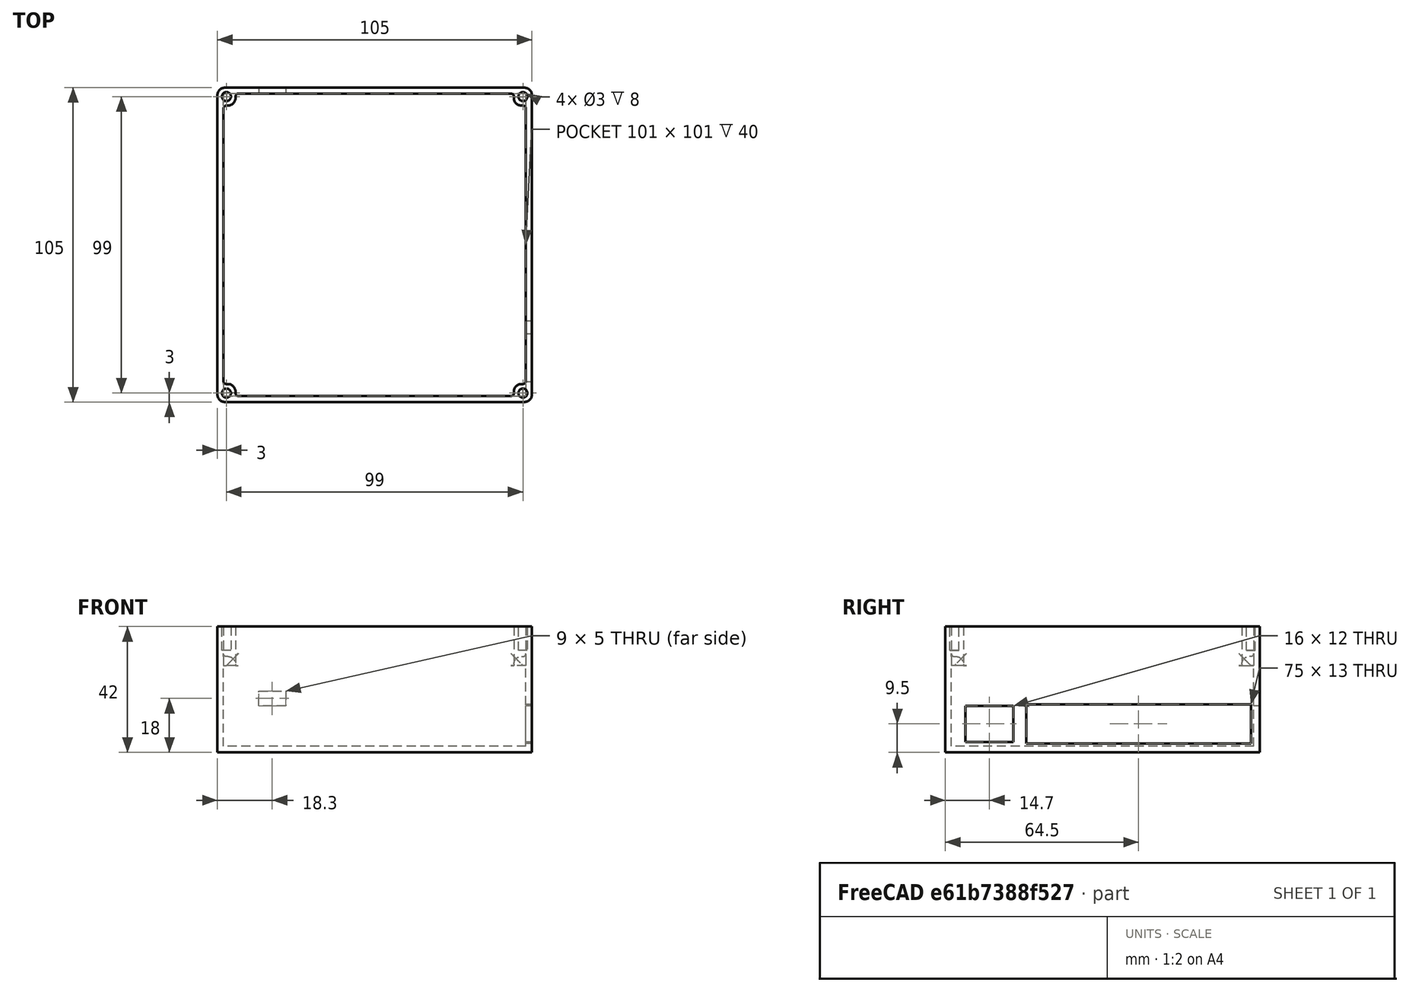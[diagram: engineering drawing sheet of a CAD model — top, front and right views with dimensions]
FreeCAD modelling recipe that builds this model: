
FCSTD DOCUMENT  (FreeCAD 0.19RUnknown)
Label: gdas_frame
License: All rights reserved
LicenseURL: http://en.wikipedia.org/wiki/All_rights_reserved
objects: Sketcher::SketchObject×6, PartDesign::Pad×3, PartDesign::Pocket×3, PartDesign::Fillet×3, PartDesign::Body×2, Mesh::Feature×1, App::MeasureDistance×1, PartDesign::Plane×1, PartDesign::Chamfer×1
note: 29 computed .brp shape members not serialized (recipe doc carries the construction recipe); baked Part::Feature solids carry a one-line shape summary decoded from their .brp

FEATURE [Mesh::Feature] OBJ_PCB_v2
  Placement = pos=(-1028.5,987.5,3) rot=(0,0,1;0rad)
FEATURE [PartDesign::Body] Body
  Origin = -> Origin
FEATURE [App::MeasureDistance] Distance  label="Distance: 97.20 mm"
  Distance = 97.1998
  P1 = (-48.7548,48.251,2.5)
  P2 = (48.4449,48.251,2.5)
FEATURE [Sketcher::SketchObject] Sketch
  MapMode = 5
  Support = -> [XY_Plane001]
  sketch-geometry (4):
    g0: LineSegment StartX=0 StartY=105 StartZ=0 EndX=105 EndY=105 EndZ=0
    g1: LineSegment StartX=105 StartY=105 StartZ=0 EndX=105 EndY=0 EndZ=0
    g2: LineSegment StartX=105 StartY=0 StartZ=0 EndX=0 EndY=0 EndZ=0
    g3: LineSegment StartX=0 StartY=0 StartZ=0 EndX=0 EndY=105 EndZ=0
  constraints (11):
    c: Coincident(g0,g1)
    c: Coincident(g1,g2)
    c: Coincident(g2,g3)
    c: Coincident(g3,g0)
    c: Horizontal(g0)
    c: Horizontal(g2)
    c: Vertical(g1)
    c: Vertical(g3)
    c: Coincident(g2,g-1)
    c: Distance(g0) = 105
    c: Distance(g1) = 105
FEATURE [PartDesign::Pad] Pad
  Direction = (1,1,1)
  Length = 2
  Length2 = 100
  Profile = -> Sketch
  Refine = true
  Type = 0
FEATURE [Sketcher::SketchObject] Sketch001
  ExternalGeometry = -> [Sketch]
  MapMode = 5
  Placement = pos=(0,0,2) rot=(0,0,1;0rad)
  Support = -> [Pad]
  sketch-geometry (8):
    g0: LineSegment StartX=0 StartY=0 StartZ=0 EndX=105 EndY=0 EndZ=0
    g1: LineSegment StartX=105 StartY=0 StartZ=0 EndX=105 EndY=105 EndZ=0
    g2: LineSegment StartX=105 StartY=105 StartZ=0 EndX=0 EndY=105 EndZ=0
    g3: LineSegment StartX=0 StartY=105 StartZ=0 EndX=0 EndY=0 EndZ=0
    g4: LineSegment StartX=2 StartY=2 StartZ=0 EndX=103 EndY=2 EndZ=0
    g5: LineSegment StartX=103 StartY=2 StartZ=0 EndX=103 EndY=103 EndZ=0
    g6: LineSegment StartX=103 StartY=103 StartZ=0 EndX=2 EndY=103 EndZ=0
    g7: LineSegment StartX=2 StartY=103 StartZ=0 EndX=2 EndY=2 EndZ=0
  constraints (22):
    c: Coincident(g0,g1)
    c: Coincident(g1,g2)
    c: Coincident(g2,g3)
    c: Coincident(g3,g0)
    c: Horizontal(g0)
    c: Horizontal(g2)
    c: Vertical(g1)
    c: Vertical(g3)
    c: Coincident(g0,g-1)
    c: Coincident(g1,g-3)
    c: Coincident(g4,g5)
    c: Coincident(g5,g6)
    c: Coincident(g6,g7)
    c: Coincident(g7,g4)
    c: Horizontal(g4)
    c: Horizontal(g6)
    c: Vertical(g5)
    c: Vertical(g7)
    c: Distance(g5) = 101
    c: Distance(g4) = 101
    c: DistanceX(g0,g4) = 2
    c: DistanceY(g0,g4) = 2
FEATURE [PartDesign::Pad] Pad001
  BaseFeature = -> Pad
  Direction = (1,1,1)
  Length = 40
  Length2 = 100
  Profile = -> Sketch001
  Refine = true
  Type = 0
FEATURE [Sketcher::SketchObject] Sketch002
  ExternalGeometry = -> [Pad001,Sketch]
  MapMode = 5
  Placement = pos=(105,0,0) rot=(0.57735,0.57735,0.57735;2.0944rad)
  Support = -> [Pad001]
  sketch-geometry (8):
    g0: LineSegment StartX=27 StartY=16 StartZ=0 EndX=102 EndY=16 EndZ=0
    g1: LineSegment StartX=102 StartY=16 StartZ=0 EndX=102 EndY=3 EndZ=0
    g2: LineSegment StartX=102 StartY=3 StartZ=0 EndX=27 EndY=3 EndZ=0
    g3: LineSegment StartX=27 StartY=3 StartZ=0 EndX=27 EndY=16 EndZ=0
    g4: LineSegment StartX=6.7 StartY=15.5 StartZ=0 EndX=22.7 EndY=15.5 EndZ=0
    g5: LineSegment StartX=22.7 StartY=15.5 StartZ=0 EndX=22.7 EndY=3.5 EndZ=0
    g6: LineSegment StartX=22.7 StartY=3.5 StartZ=0 EndX=6.7 EndY=3.5 EndZ=0
    g7: LineSegment StartX=6.7 StartY=3.5 StartZ=0 EndX=6.7 EndY=15.5 EndZ=0
  constraints (24):
    c: Coincident(g0,g1)
    c: Coincident(g1,g2)
    c: Coincident(g2,g3)
    c: Coincident(g3,g0)
    c: Horizontal(g0)
    c: Horizontal(g2)
    c: Vertical(g1)
    c: Vertical(g3)
    c: DistanceY(g-5,g1) = 3
    c: Distance(g1) = 13
    c: Distance(g0) = 75
    c: DistanceX(g1,g-5) = 3
    c: Coincident(g4,g5)
    c: Coincident(g5,g6)
    c: Coincident(g6,g7)
    c: Coincident(g7,g4)
    c: Horizontal(g4)
    c: Horizontal(g6)
    c: Vertical(g5)
    c: Vertical(g7)
    c: DistanceX(g-1,g6) = 6.7
    c: DistanceY(g-1,g6) = 3.5
    c: Distance(g4) = 16
    c: Distance(g7) = 12
FEATURE [PartDesign::Pocket] Pocket
  BaseFeature = -> Pad001
  Length = 0
  Length2 = 100
  Profile = -> Sketch002
  Refine = true
  Type = 2
FEATURE [Sketcher::SketchObject] Sketch003
  ExternalGeometry = -> [Pocket,Sketch]
  MapMode = 5
  Placement = pos=(0,105,0) rot=(0,0.707107,0.707107;3.14159rad)
  Support = -> [Pocket]
  sketch-geometry (4):
    g0: LineSegment StartX=-22.8 StartY=20.5 StartZ=0 EndX=-13.8 EndY=20.5 EndZ=0
    g1: LineSegment StartX=-13.8 StartY=20.5 StartZ=0 EndX=-13.8 EndY=15.5 EndZ=0
    g2: LineSegment StartX=-13.8 StartY=15.5 StartZ=0 EndX=-22.8 EndY=15.5 EndZ=0
    g3: LineSegment StartX=-22.8 StartY=15.5 StartZ=0 EndX=-22.8 EndY=20.5 EndZ=0
  constraints (12):
    c: Coincident(g0,g1)
    c: Coincident(g1,g2)
    c: Coincident(g2,g3)
    c: Coincident(g3,g0)
    c: Horizontal(g0)
    c: Horizontal(g2)
    c: Vertical(g1)
    c: Vertical(g3)
    c: DistanceX(g0,g0) = 9
    c: Distance(g1) = 5
    c: DistanceX(g1,g-1) = 13.8
    c: DistanceY(g-1,g1) = 15.5
FEATURE [PartDesign::Pocket] Pocket001
  BaseFeature = -> Pocket
  Length = 5
  Length2 = 100
  Profile = -> Sketch003
  Refine = true
  Type = 2
FEATURE [PartDesign::Plane] DatumPlane
  Length = 156
  MapMode = 5
  Placement = pos=(0,0,42) rot=(0,0,1;0rad)
  ResizeMode = 0
  Support = -> [Pocket001]
  Width = 156
FEATURE [Sketcher::SketchObject] Sketch004
  ExternalGeometry = -> [Pocket001]
  MapMode = 5
  Placement = pos=(0,0,42) rot=(0,0,1;0rad)
  Support = -> [Pocket001]
  sketch-geometry (16):
    g0: LineSegment StartX=103 StartY=103 StartZ=0 EndX=99 EndY=103 EndZ=0
    g1: LineSegment StartX=99 StartY=103 StartZ=0 EndX=99 EndY=99 EndZ=0
    g2: LineSegment StartX=99 StartY=99 StartZ=0 EndX=103 EndY=99 EndZ=0
    g3: LineSegment StartX=103 StartY=99 StartZ=0 EndX=103 EndY=103 EndZ=0
    g4: LineSegment StartX=103 StartY=2 StartZ=0 EndX=99 EndY=2 EndZ=0
    g5: LineSegment StartX=99 StartY=2 StartZ=0 EndX=99 EndY=6 EndZ=0
    g6: LineSegment StartX=99 StartY=6 StartZ=0 EndX=103 EndY=6 EndZ=0
    g7: LineSegment StartX=103 StartY=6 StartZ=0 EndX=103 EndY=2 EndZ=0
    g8: LineSegment StartX=2 StartY=2 StartZ=0 EndX=6 EndY=2 EndZ=0
    g9: LineSegment StartX=6 StartY=2 StartZ=0 EndX=6 EndY=6 EndZ=0
    g10: LineSegment StartX=6 StartY=6 StartZ=0 EndX=2 EndY=6 EndZ=0
    g11: LineSegment StartX=2 StartY=6 StartZ=0 EndX=2 EndY=2 EndZ=0
    g12: LineSegment StartX=2 StartY=103 StartZ=0 EndX=6 EndY=103 EndZ=0
    g13: LineSegment StartX=6 StartY=103 StartZ=0 EndX=6 EndY=99 EndZ=0
    g14: LineSegment StartX=6 StartY=99 StartZ=0 EndX=2 EndY=99 EndZ=0
    g15: LineSegment StartX=2 StartY=99 StartZ=0 EndX=2 EndY=103 EndZ=0
  constraints (44):
    c: Coincident(g0,g1)
    c: Coincident(g1,g2)
    c: Coincident(g2,g3)
    c: Coincident(g3,g0)
    c: Horizontal(g0)
    c: Horizontal(g2)
    c: Vertical(g1)
    c: Vertical(g3)
    c: Coincident(g0,g-4)
    c: Coincident(g4,g5)
    c: Coincident(g5,g6)
    c: Coincident(g6,g7)
    c: Coincident(g7,g4)
    c: Horizontal(g4)
    c: Horizontal(g6)
    c: Vertical(g5)
    c: Vertical(g7)
    c: Coincident(g4,g-5)
    c: Coincident(g8,g9)
    c: Coincident(g9,g10)
    c: Coincident(g10,g11)
    c: Coincident(g11,g8)
    c: Horizontal(g8)
    c: Horizontal(g10)
    c: Vertical(g9)
    c: Vertical(g11)
    c: Coincident(g8,g-6)
    c: Coincident(g12,g13)
    c: Coincident(g13,g14)
    c: Coincident(g14,g15)
    c: Coincident(g15,g12)
    c: Horizontal(g12)
    c: Horizontal(g14)
    c: Vertical(g13)
    c: Vertical(g15)
    c: Coincident(g12,g-6)
    c: Distance(g13) = 4
    c: Equal(g13,g1)
    c: Equal(g13,g14)
    c: Equal(g1,g2)
    c: Equal(g2,g6)
    c: Equal(g6,g5)
    c: Equal(g6,g10)
    c: Equal(g9,g10)
FEATURE [PartDesign::Pad] Pad002
  BaseFeature = -> Pocket001
  Direction = (-0.1,-0.1,0.9)
  Length = 13
  Length2 = 100
  Profile = -> Sketch004
  Refine = true
  Reversed = true
  Type = 0
FEATURE [Sketcher::SketchObject] Sketch005
  ExternalGeometry = -> [Pad002]
  MapMode = 5
  Placement = pos=(0,0,42) rot=(0,0,1;0rad)
  Support = -> [DatumPlane]
  sketch-geometry (4):
    g0: Circle CenterX=3 CenterY=102 CenterZ=0 NormalX=0 NormalY=0 NormalZ=1 AngleXU=0 Radius=1.5
    g1: Circle CenterX=3 CenterY=3 CenterZ=0 NormalX=0 NormalY=0 NormalZ=1 AngleXU=0 Radius=1.5
    g2: Circle CenterX=102 CenterY=3 CenterZ=0 NormalX=0 NormalY=0 NormalZ=1 AngleXU=0 Radius=1.5
    g3: Circle CenterX=102 CenterY=102 CenterZ=0 NormalX=0 NormalY=0 NormalZ=1 AngleXU=0 Radius=1.5
  constraints (12):
    c: Diameter(g0) = 3
    c: DistanceX(g0,g-4) = 3
    c: DistanceY(g-4,g0) = 3
    c: Equal(g3,g0)
    c: Equal(g2,g3)
    c: Equal(g1,g2)
    c: DistanceY(g1,g-10) = 3
    c: DistanceX(g1,g-10) = 3
    c: DistanceX(g-8,g2) = 3
    c: DistanceX(g-6,g3) = 3
    c: DistanceY(g-6,g3) = 3
    c: DistanceY(g2,g-8) = 3
FEATURE [PartDesign::Pocket] Pocket002
  BaseFeature = -> Pad002
  Length = 8
  Length2 = 100
  Profile = -> Sketch005
  Refine = true
  Type = 0
FEATURE [PartDesign::Fillet] Fillet
  Base = -> Pocket002 [Edge4,Edge36,Edge1,Edge5]
  BaseFeature = -> Pocket002
  Radius = 2.5
  Refine = true
  SupportTransform = false
FEATURE [PartDesign::Chamfer] Chamfer
  Angle = 45
  Base = -> Fillet [Edge93,Edge71,Edge69,Edge91]
  BaseFeature = -> Fillet
  ChamferType = 0
  FlipDirection = false
  Refine = true
  Size = 3
  Size2 = 1
  SupportTransform = false
FEATURE [PartDesign::Fillet] Fillet001
  Base = -> Chamfer [Edge78,Edge22,Edge57,Edge114]
  BaseFeature = -> Chamfer
  Radius = 2.5
  Refine = true
  SupportTransform = false
FEATURE [PartDesign::Fillet] Fillet002
  Base = -> Fillet001 [Edge55,Edge20,Edge57,Edge76,Edge49,Edge81,Edge9,Edge14]
  BaseFeature = -> Fillet001
  Radius = 1
  Refine = true
  SupportTransform = false
FEATURE [PartDesign::Body] Body001
  Group = -> [Sketch,Pad,Sketch001,Pad001,Sketch002,Pocket,Sketch003,Pocket001,DatumPlane,Sketch004,Pad002,Sketch005,Pocket002,Fillet,Chamfer,Fillet001,Fillet002]
  Origin = -> Origin001
  Tip = -> Fillet002
